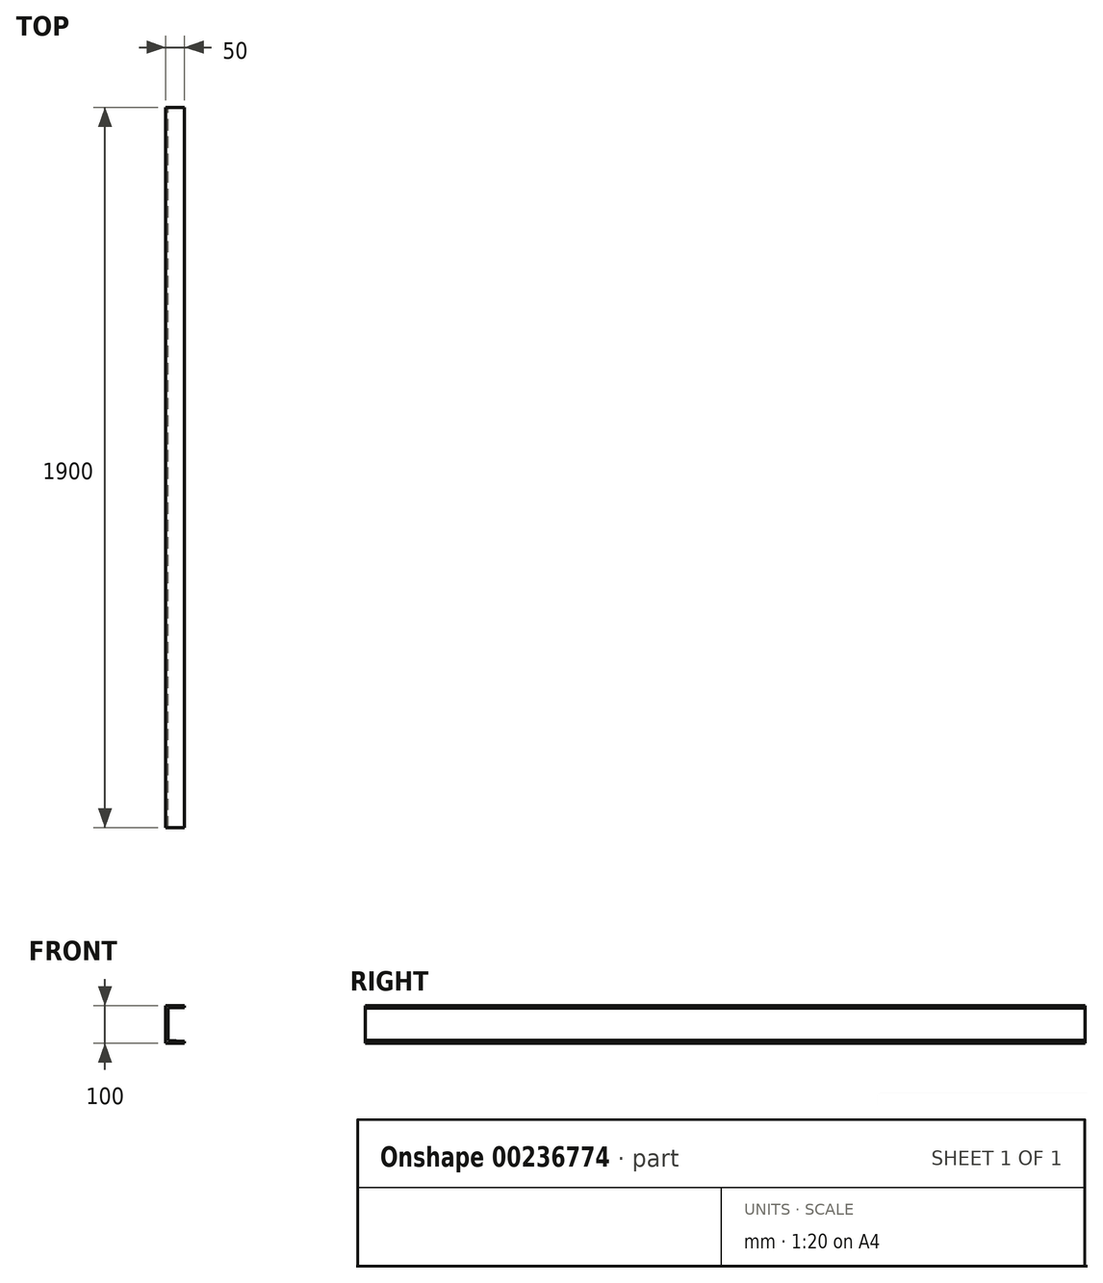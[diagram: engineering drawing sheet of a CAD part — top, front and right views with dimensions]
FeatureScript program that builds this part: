
annotation { "Feature Type Name" : "Feature", "Feature Type Description" : "" }
export const myFeature = defineFeature(function(context is Context, id is Id, definition is map)
    precondition{}
    {
        {
            var Q0;
            Q0=qCreatedBy(makeId("Front.planeOp"),FACE);
            var sketch = newSketch(context, id + "F0", { "sketchPlane" : qUnion([Q0])});
            skLineSegment(sketch, "E0.bottom", {"start": v(0, 0) * mm, "end": v(50, 0) * mm});
            skLineSegment(sketch, "E0.top", {"start": v(0, 100) * mm, "end": v(50, 100) * mm});
            skLineSegment(sketch, "E0.left", {"start": v(0, 0) * mm, "end": v(0, 100) * mm});
            skLineSegment(sketch, "E0.right", {"start": v(50, 0) * mm, "end": v(50, 5) * mm});
            skLineSegment(sketch, "E1.left", {"start": v(4.68, 71.03) * mm, "end": v(4.68, 71.03) * mm});
            skLineSegment(sketch, "E1.right", {"start": v(12.2, 71.03) * mm, "end": v(12.2, 71.03) * mm});
            skLineSegment(sketch, "E2", {"start": v(6, 8.46) * mm, "end": v(50, 5) * mm});
            skLineSegment(sketch, "E3", {"start": v(6, 8.46) * mm, "end": v(6, 93.46) * mm});
            skLineSegment(sketch, "E4", {"start": v(6, 93.46) * mm, "end": v(50, 95) * mm});
            skLineSegment(sketch, "E5.trimOffspring", {"start": v(50, 95) * mm, "end": v(50, 100) * mm});
            skSolve(sketch);
        }
        {
            var Q0;
            Q0=makeQuery(id+"F0.imprint","IMPRINT",FACE,{"disambiguationData":[TD([[makeQuery(id+"F0.imprint","IMPRINT",EDGE,{"derivedFrom":sQuery(id+"F0.wireOp",EDGE,"E0.bottom")}),1.0]])]});
            extrude(context, id + "F1", {"entities" : qUnion([Q0]), "depth" : 1900 * mm, "offsetDistance" : 25 * mm});
        }
    });
